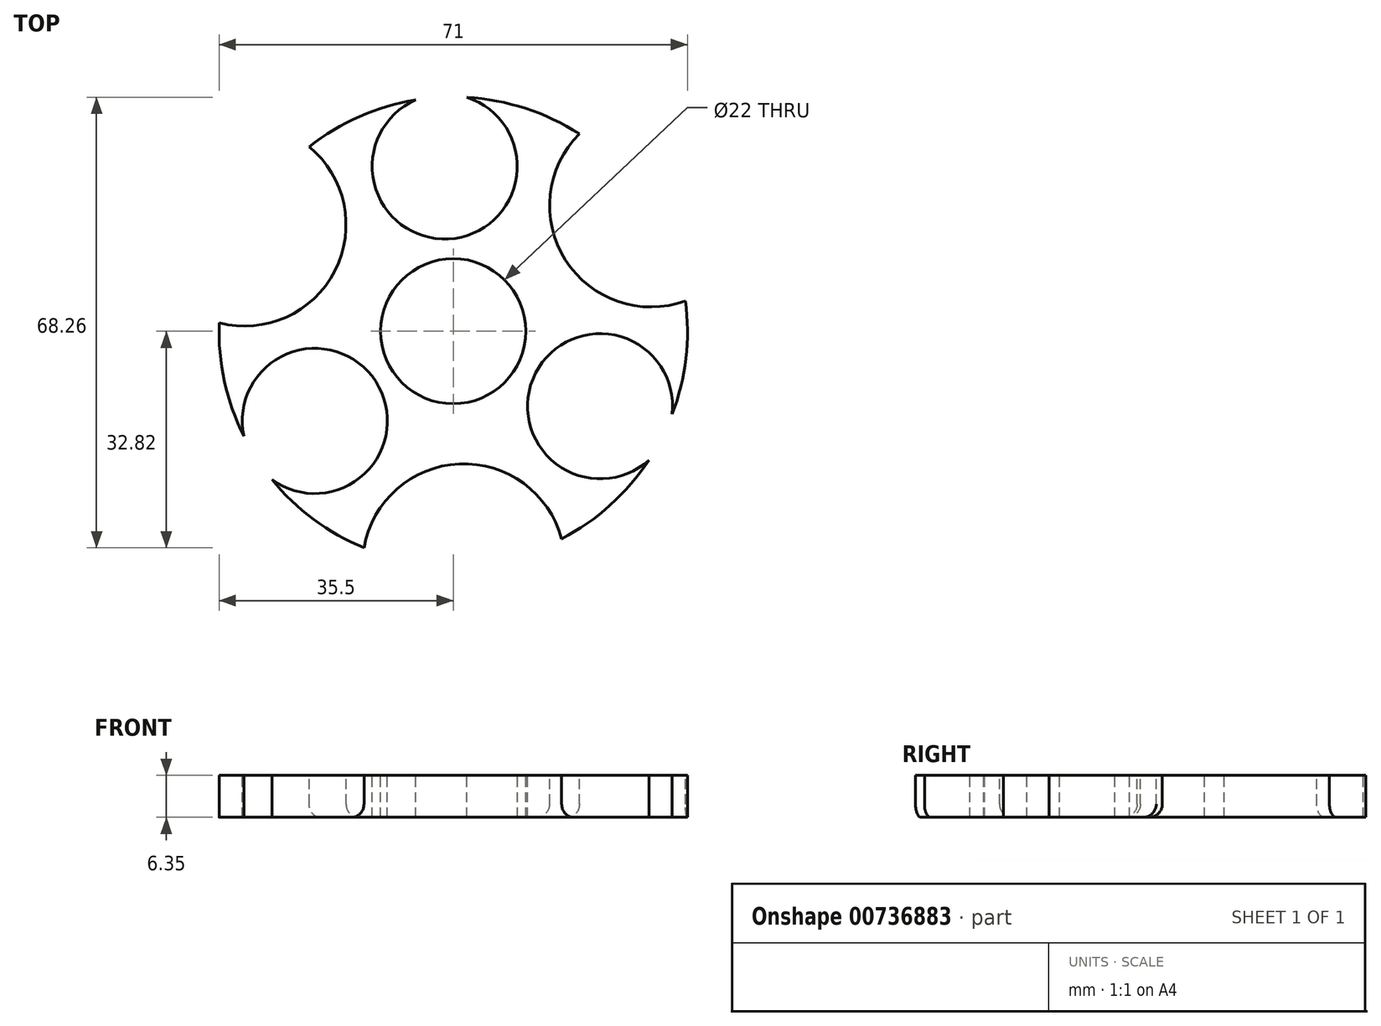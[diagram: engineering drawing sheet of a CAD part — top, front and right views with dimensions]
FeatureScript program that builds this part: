
annotation { "Feature Type Name" : "Feature", "Feature Type Description" : "" }
export const myFeature = defineFeature(function(context is Context, id is Id, definition is map)
    precondition{}
    {
        {
            var Q0;
            Q0=qCreatedBy(makeId("Top.planeOp"),FACE);
            var sketch = newSketch(context, id + "F0", { "sketchPlane" : qUnion([Q0])});
            skCircle(sketch, "E0", {"center": v(0, 0) * mm, "radius": 35.5 * mm});
            skSolve(sketch);
        }
        {
            var Q0;
            Q0=makeQuery(id+"F0.imprint","IMPRINT",FACE,{"disambiguationData":[TD([[makeQuery(id+"F0.imprint","IMPRINT",EDGE,{"derivedFrom":sQuery(id+"F0.wireOp",EDGE,"E0")}),1.0]])]});
            extrude(context, id + "F1", {"entities" : qUnion([Q0]), "depth" : 6.35 * mm, "offsetDistance" : 25 * mm});
        }
        {
            var Q0;
            {var subQ0=sQuery(id+"F0.wireOp",EDGE,"E0");Q0=makeQuery(id+"F1.opExtrude","CAP_FACE",FACE,{"disambiguationData":[OSD([subQ0]),TDD([makeQuery(id+"F0.imprint","IMPRINT",EDGE,{"derivedFrom":subQ0})])],"isStart":false});}
            var sketch = newSketch(context, id + "F2", { "sketchPlane" : qUnion([Q0])});
            skCircle(sketch, "E1", {"center": v(-1.29, 24.97) * mm, "radius": 11 * mm});
            skCircle(sketch, "E2", {"center": v(22.26, -11.37) * mm, "radius": 11 * mm});
            skCircle(sketch, "E3", {"center": v(-20.98, -13.6) * mm, "radius": 11 * mm});
            skCircle(sketch, "E4", {"center": v(0, 0) * mm, "radius": 11 * mm});
            skArc(sketch, "E5", {"start": v(16.44, -31.47) * mm, "mid": v(0.9, -20.12) * mm, "end": v(-13.53, -32.82) * mm});
            skArc(sketch, "E6", {"start": v(19.12, 29.91) * mm, "mid": v(17, 10.8) * mm, "end": v(35.2, 4.59) * mm});
            skArc(sketch, "E7", {"start": v(-35.48, 1.26) * mm, "mid": v(-17.94, 9.15) * mm, "end": v(-21.84, 27.99) * mm});
            skSolve(sketch);
        }
        {
            var Q0;
            {var subQ0=sQuery(id+"F2.wireOp",EDGE,"E7");Q0=makeQuery(id+"F2.imprint","IMPRINT",FACE,{"disambiguationData":[TD([[makeQuery(id+"F2.imprint","IMPRINT",EDGE,{"derivedFrom":subQ0}),1.0]])]});}
            var Q1;
            Q1=makeQuery(id+"F2.imprint","IMPRINT",FACE,{"disambiguationData":[TD([[makeQuery(id+"F2.imprint","IMPRINT",EDGE,{"derivedFrom":sQuery(id+"F2.wireOp",EDGE,"E1")}),1.0]])]});
            var Q2;
            Q2=makeQuery(id+"F2.imprint","IMPRINT",FACE,{"disambiguationData":[TD([[makeQuery(id+"F2.imprint","IMPRINT",EDGE,{"derivedFrom":sQuery(id+"F2.wireOp",EDGE,"E4")}),1.0]])]});
            var Q3;
            {var subQ0=sQuery(id+"F2.wireOp",EDGE,"E6");Q3=makeQuery(id+"F2.imprint","IMPRINT",FACE,{"disambiguationData":[TD([[makeQuery(id+"F2.imprint","IMPRINT",EDGE,{"derivedFrom":subQ0}),1.0]])]});}
            var Q4;
            Q4=makeQuery(id+"F2.imprint","IMPRINT",FACE,{"disambiguationData":[TD([[makeQuery(id+"F2.imprint","IMPRINT",EDGE,{"derivedFrom":sQuery(id+"F2.wireOp",EDGE,"E2")}),1.0]])]});
            var Q5;
            {var subQ0=sQuery(id+"F2.wireOp",EDGE,"E5");Q5=makeQuery(id+"F2.imprint","IMPRINT",FACE,{"disambiguationData":[TD([[makeQuery(id+"F2.imprint","IMPRINT",EDGE,{"derivedFrom":subQ0}),1.0]])]});}
            var Q6;
            Q6=makeQuery(id+"F2.imprint","IMPRINT",FACE,{"disambiguationData":[TD([[makeQuery(id+"F2.imprint","IMPRINT",EDGE,{"derivedFrom":sQuery(id+"F2.wireOp",EDGE,"E3")}),1.0]])]});
            extrude(context, id + "F3", {"entities" : qUnion([Q0, Q1, Q2, Q3, Q4, Q5, Q6]), "operationType" : NewBodyOperationType.REMOVE, "oppositeDirection" : true, "depth" : 45.4 * mm, "offsetDistance" : 25 * mm});
        }
        {
            var Q0;
            Q0=makeQuery(id+"F3.boolean.opBoolean","INTERSECT",EDGE,{"derivedFrom":[makeQuery(id+"F1.opExtrude","CAP_FACE",FACE,{"disambiguationData":[OSD([sQuery(id+"F0.wireOp",EDGE,"E0")])],"isStart":true}),makeQuery(id+"F3.opExtrude","SWEPT_FACE",FACE,{"disambiguationData":[OSD([sQuery(id+"F2.wireOp",EDGE,"E7")])]})]});
            var Q1;
            Q1=makeQuery(id+"F3.boolean.opBoolean","COPY",EDGE,{"derivedFrom":makeQuery(id+"F3.opExtrude","CAP_EDGE",EDGE,{"disambiguationData":[OSD([sQuery(id+"F2.wireOp",EDGE,"E7")])],"isStart":true})});
            var Q2;
            Q2=makeQuery(id+"F3.boolean.opBoolean","INTERSECT",EDGE,{"derivedFrom":[makeQuery(id+"F1.opExtrude","CAP_FACE",FACE,{"disambiguationData":[OSD([sQuery(id+"F0.wireOp",EDGE,"E0")])],"isStart":true}),makeQuery(id+"F3.opExtrude","SWEPT_FACE",FACE,{"disambiguationData":[OSD([sQuery(id+"F2.wireOp",EDGE,"E6")])]})]});
            var Q3;
            Q3=makeQuery(id+"F3.boolean.opBoolean","COPY",EDGE,{"derivedFrom":makeQuery(id+"F3.opExtrude","CAP_EDGE",EDGE,{"disambiguationData":[OSD([sQuery(id+"F2.wireOp",EDGE,"E6")])],"isStart":true})});
            var Q4;
            Q4=makeQuery(id+"F3.boolean.opBoolean","INTERSECT",EDGE,{"derivedFrom":[makeQuery(id+"F1.opExtrude","CAP_FACE",FACE,{"disambiguationData":[OSD([sQuery(id+"F0.wireOp",EDGE,"E0")])],"isStart":true}),makeQuery(id+"F3.opExtrude","SWEPT_FACE",FACE,{"disambiguationData":[OSD([sQuery(id+"F2.wireOp",EDGE,"E5")])]})]});
            var Q5;
            Q5=makeQuery(id+"F3.boolean.opBoolean","COPY",EDGE,{"derivedFrom":makeQuery(id+"F3.opExtrude","CAP_EDGE",EDGE,{"disambiguationData":[OSD([sQuery(id+"F2.wireOp",EDGE,"E5")])],"isStart":true})});
            fillet(context, id + "F4", {"entities" : qUnion([Q0, Q1, Q2, Q3, Q4, Q5]), "radius" : 2 * mm, "tangentPropagation" : true, "allowEdgeOverflow" : false});
        }
    });
